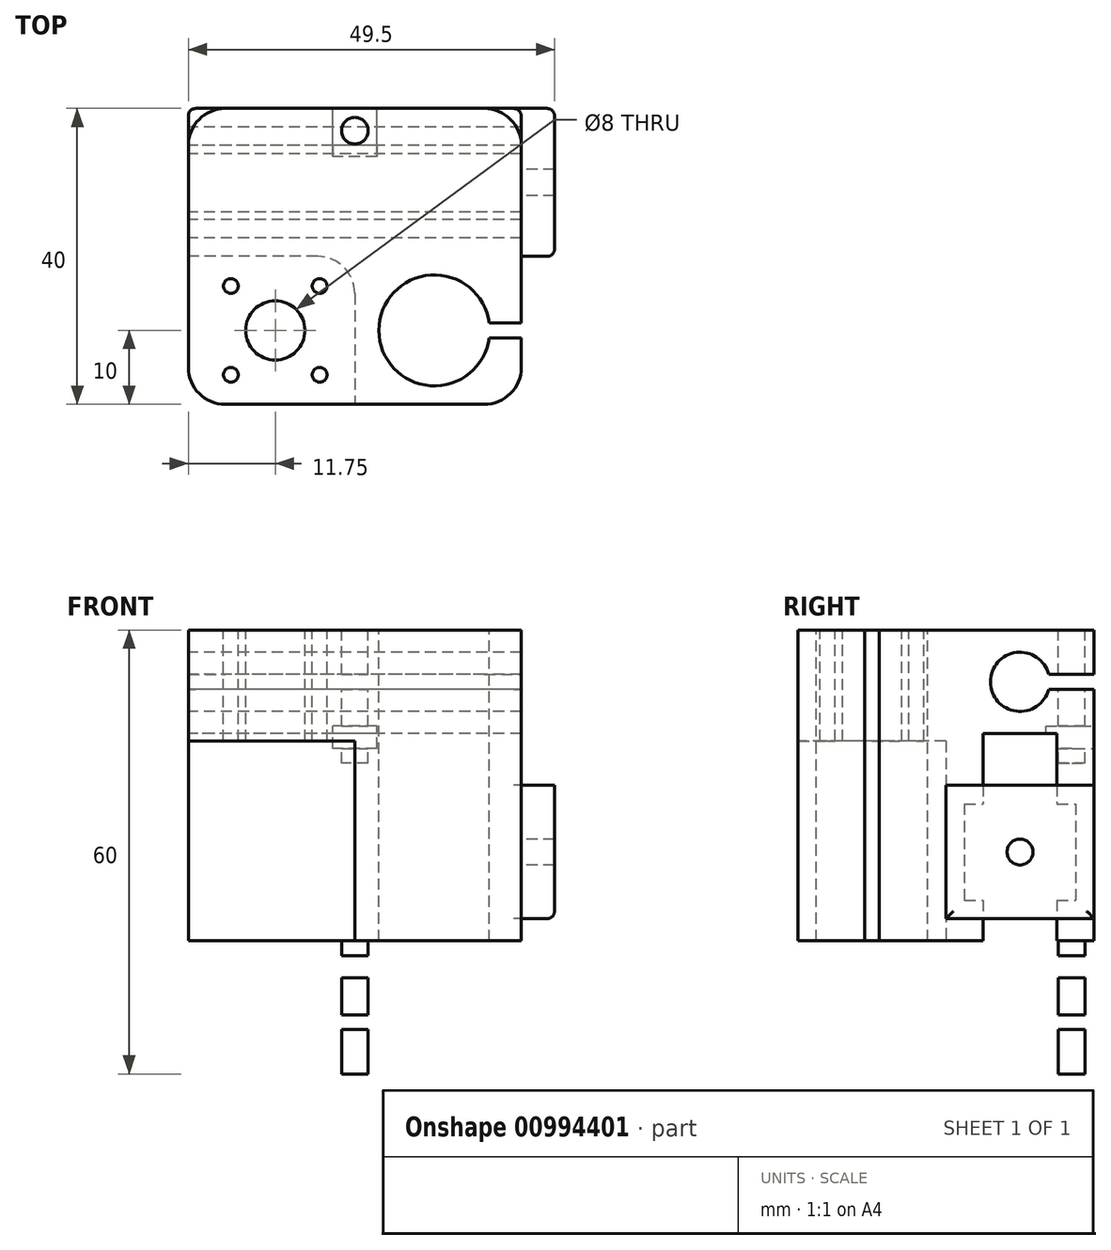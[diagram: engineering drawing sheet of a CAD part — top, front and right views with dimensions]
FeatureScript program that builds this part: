
annotation { "Feature Type Name" : "Feature", "Feature Type Description" : "" }
export const myFeature = defineFeature(function(context is Context, id is Id, definition is map)
    precondition{}
    {
        {
            var Q0;
            Q0=qCreatedBy(makeId("Top.planeOp"),FACE);
            var sketch = newSketch(context, id + "F0", { "sketchPlane" : qUnion([Q0])});
            skLineSegment(sketch, "E0.bottom", {"start": v(0, 0) * mm, "end": v(-45, 0) * mm});
            skLineSegment(sketch, "E0.top", {"start": v(0, 40) * mm, "end": v(-45, 40) * mm});
            skLineSegment(sketch, "E0.left", {"start": v(0, 0) * mm, "end": v(0, 40) * mm});
            skLineSegment(sketch, "E0.right", {"start": v(-45, 0) * mm, "end": v(-45, 40) * mm});
            skSolve(sketch);
        }
        {
            var Q0;
            Q0 = qSketchRegion(id + "F0", true);
            extrude(context, id + "F1", {"entities" : qUnion([Q0]), "depth" : 60 * mm, "offsetDistance" : 25 * mm});
        }
        {
            var Q0;
            Q0=makeQuery(id+"F1.opExtrude","CAP_FACE",FACE,{"disambiguationData":[OSD([sQuery(id+"F0.wireOp",EDGE,"E0.bottom"),sQuery(id+"F0.wireOp",EDGE,"E0.top"),sQuery(id+"F0.wireOp",EDGE,"E0.left"),sQuery(id+"F0.wireOp",EDGE,"E0.right")])],"isStart":false});
            var sketch = newSketch(context, id + "F2", { "sketchPlane" : qUnion([Q0])});
            skLineSegment(sketch, "E1", {"start": v(-45, 20) * mm, "end": v(0, 20) * mm});
            skLineSegment(sketch, "E2", {"start": v(0, 20) * mm, "end": v(-45, 0) * mm, "construction": true});
            skCircle(sketch, "E3", {"center": v(-33.25, 10) * mm, "radius": 4 * mm});
            skCircle(sketch, "E4", {"center": v(-11.75, 10) * mm, "radius": 4 * mm});
            skPoint(sketch, "E5", {"position": v(-22.5, 10) * mm});
            skPoint(sketch, "E6.0", {"position": v(-22.5, 0) * mm});
            skCircle(sketch, "E7", {"center": v(-11.75, 10) * mm, "radius": 7.5 * mm});
            skCircle(sketch, "E8", {"center": v(-39.25, 16) * mm, "radius": 1 * mm});
            skCircle(sketch, "E9", {"center": v(-27.25, 16) * mm, "radius": 1 * mm});
            skCircle(sketch, "E10", {"center": v(-27.25, 4) * mm, "radius": 1 * mm});
            skCircle(sketch, "E11", {"center": v(-39.25, 4) * mm, "radius": 1 * mm});
            skLineSegment(sketch, "E12", {"start": v(-39.25, 16) * mm, "end": v(-27.25, 4) * mm, "construction": true});
            skLineSegment(sketch, "E13", {"start": v(-4.25, 10) * mm, "end": v(0, 10) * mm});
            skLineSegment(sketch, "E14.0", {"start": v(-4.32, 9) * mm, "end": v(0, 9) * mm});
            skLineSegment(sketch, "E15.0", {"start": v(-4.32, 11) * mm, "end": v(0, 11) * mm});
            skCircle(sketch, "E16", {"center": v(-22.5, 37) * mm, "radius": 1.8 * mm});
            skPoint(sketch, "E16.centerSnap0", {"position": v(-22.5, 40) * mm});
            skSolve(sketch);
        }
        {
            var Q0;
            Q0=makeQuery(id+"F1.opExtrude","SWEPT_FACE",FACE,{"disambiguationData":[OSD([sQuery(id+"F0.wireOp",EDGE,"E0.right")])]});
            var sketch = newSketch(context, id + "F3", { "sketchPlane" : qUnion([Q0])});
            skLineSegment(sketch, "E17.0.0", {"start": v(-40, 0) * mm, "end": v(0, 0) * mm});
            skLineSegment(sketch, "E17.0.1", {"start": v(0, 0) * mm, "end": v(0, 60) * mm});
            skLineSegment(sketch, "E17.0.2", {"start": v(0, 60) * mm, "end": v(-40, 60) * mm});
            skLineSegment(sketch, "E17.0.3", {"start": v(-40, 60) * mm, "end": v(-40, 0) * mm});
            skLineSegment(sketch, "E18", {"start": v(-20, 60) * mm, "end": v(-20, 0) * mm});
            skLineSegment(sketch, "E19", {"start": v(-20, 60) * mm, "end": v(-40, 0) * mm, "construction": true});
            skArc(sketch, "E20", {"start": v(-33.87, 52) * mm, "mid": v(-26, 53) * mm, "end": v(-33.87, 54) * mm});
            skArc(sketch, "E21", {"start": v(-33.87, 6) * mm, "mid": v(-26, 7) * mm, "end": v(-33.87, 8) * mm});
            skPoint(sketch, "E22", {"position": v(-30, 30) * mm});
            skPoint(sketch, "E23", {"position": v(-40, 30) * mm});
            skLineSegment(sketch, "E24", {"start": v(-20, 45) * mm, "end": v(0, 45) * mm});
            skLineSegment(sketch, "E25.bottom", {"start": v(-25, 46) * mm, "end": v(-35, 46) * mm});
            skLineSegment(sketch, "E25.top", {"start": v(-25, 14) * mm, "end": v(-35, 14) * mm});
            skLineSegment(sketch, "E25.left", {"start": v(-25, 46) * mm, "end": v(-25, 14) * mm});
            skLineSegment(sketch, "E25.right", {"start": v(-35, 46) * mm, "end": v(-35, 14) * mm});
            skPoint(sketch, "E26", {"position": v(-30, 46) * mm});
            skLineSegment(sketch, "E27.bottom", {"start": v(-22.5, 36.5) * mm, "end": v(-37.5, 36.5) * mm});
            skLineSegment(sketch, "E27.top", {"start": v(-22.5, 23.5) * mm, "end": v(-37.5, 23.5) * mm});
            skLineSegment(sketch, "E27.left", {"start": v(-22.5, 36.5) * mm, "end": v(-22.5, 23.5) * mm});
            skLineSegment(sketch, "E27.right", {"start": v(-37.5, 36.5) * mm, "end": v(-37.5, 23.5) * mm});
            skPoint(sketch, "E28", {"position": v(-30, 36.5) * mm});
            skPoint(sketch, "E29", {"position": v(-37.5, 30) * mm});
            skLineSegment(sketch, "E30.bottom", {"start": v(-40, 52) * mm, "end": v(-33.87, 52) * mm});
            skLineSegment(sketch, "E30.top", {"start": v(-40, 54) * mm, "end": v(-33.87, 54) * mm});
            skLineSegment(sketch, "E30.left", {"start": v(-40, 52) * mm, "end": v(-40, 54) * mm});
            skLineSegment(sketch, "E30.right", {"start": v(-33.87, 52) * mm, "end": v(-33.87, 54) * mm});
            skLineSegment(sketch, "E31.bottom", {"start": v(-33.87, 6) * mm, "end": v(-40, 6) * mm});
            skLineSegment(sketch, "E31.top", {"start": v(-33.87, 8) * mm, "end": v(-40, 8) * mm});
            skLineSegment(sketch, "E31.left", {"start": v(-33.87, 6) * mm, "end": v(-33.87, 8) * mm});
            skLineSegment(sketch, "E31.right", {"start": v(-40, 6) * mm, "end": v(-40, 8) * mm});
            skSolve(sketch);
        }
        {
            var Q0;
            Q0=makeQuery(id+"F3.imprint","IMPRINT",FACE,{"disambiguationData":[TD([[makeQuery(id+"F3.imprint","IMPRINT",EDGE,{"derivedFrom":sQuery(id+"F3.wireOp",EDGE,"E20")}),1.0]])]});
            var Q1;
            Q1=makeQuery(id+"F3.imprint","IMPRINT",FACE,{"disambiguationData":[TD([[makeQuery(id+"F3.imprint","IMPRINT",EDGE,{"derivedFrom":sQuery(id+"F3.wireOp",EDGE,"E21")}),1.0]])]});
            var Q2;
            Q2=makeQuery(id+"F3.imprint","IMPRINT",FACE,{"disambiguationData":[TD([[makeQuery(id+"F3.imprint","IMPRINT",EDGE,{"derivedFrom":sQuery(id+"F3.wireOp",EDGE,"E25.bottom")}),1.0]])]});
            var Q3;
            {var subQ0=sQuery(id+"F3.wireOp",EDGE,"E27.bottom");var subQ1=sQuery(id+"F3.wireOp",EDGE,"E25.left");var subQ2=makeQuery(id+"F3.imprint","INTERSECT",VERTEX,{"derivedFrom":[subQ1,subQ0]});Q3=makeQuery(id+"F3.imprint","IMPRINT",FACE,{"disambiguationData":[TD([[makeQuery(id+"F3.imprint","IMPRINT",EDGE,{"disambiguationData":[TD([[subQ2,-1.0]])],"derivedFrom":subQ1}),-1.0]])]});}
            var Q4;
            {var subQ5=sQuery(id+"F3.wireOp",EDGE,"E27.left");Q4=makeQuery(id+"F3.imprint","IMPRINT",FACE,{"disambiguationData":[TD([[makeQuery(id+"F3.imprint","IMPRINT",EDGE,{"derivedFrom":subQ5}),-1.0]])]});}
            var Q5;
            {var subQ5=sQuery(id+"F3.wireOp",EDGE,"E27.right");Q5=makeQuery(id+"F3.imprint","IMPRINT",FACE,{"disambiguationData":[TD([[makeQuery(id+"F3.imprint","IMPRINT",EDGE,{"derivedFrom":subQ5}),1.0]])]});}
            var Q6;
            {var subQ0=sQuery(id+"F3.wireOp",EDGE,"E25.top");Q6=makeQuery(id+"F3.imprint","IMPRINT",FACE,{"disambiguationData":[TD([[makeQuery(id+"F3.imprint","IMPRINT",EDGE,{"derivedFrom":subQ0}),-1.0]])]});}
            var Q7;
            {var subQ0=sQuery(id+"F3.wireOp",EDGE,"E30.bottom");Q7=makeQuery(id+"F3.imprint","IMPRINT",FACE,{"disambiguationData":[TD([[makeQuery(id+"F3.imprint","IMPRINT",EDGE,{"derivedFrom":subQ0}),1.0]])]});}
            var Q8;
            {var subQ0=sQuery(id+"F3.wireOp",EDGE,"E31.bottom");Q8=makeQuery(id+"F3.imprint","IMPRINT",FACE,{"disambiguationData":[TD([[makeQuery(id+"F3.imprint","IMPRINT",EDGE,{"derivedFrom":subQ0}),-1.0]])]});}
            extrude(context, id + "F4", {"entities" : qUnion([Q0, Q1, Q2, Q3, Q4, Q5, Q6, Q7, Q8]), "operationType" : NewBodyOperationType.REMOVE, "oppositeDirection" : true, "depth" : 45 * mm, "offsetDistance" : 25 * mm});
        }
        {
            var Q0;
            {var subQ5=sQuery(id+"F3.wireOp",EDGE,"E24");Q0=makeQuery(id+"F3.imprint","IMPRINT",FACE,{"disambiguationData":[TD([[makeQuery(id+"F3.imprint","IMPRINT",EDGE,{"derivedFrom":subQ5}),-1.0]])]});}
            extrude(context, id + "F5", {"entities" : qUnion([Q0]), "operationType" : NewBodyOperationType.REMOVE, "oppositeDirection" : true, "depth" : 22.5 * mm, "offsetDistance" : 25 * mm});
        }
        {
            var Q0;
            Q0=makeQuery(id+"F2.imprint","IMPRINT",FACE,{"disambiguationData":[TD([[makeQuery(id+"F2.imprint","IMPRINT",EDGE,{"derivedFrom":sQuery(id+"F2.wireOp",EDGE,"E3")}),1.0]])]});
            var Q1;
            Q1=makeQuery(id+"F2.imprint","IMPRINT",FACE,{"disambiguationData":[TD([[makeQuery(id+"F2.imprint","IMPRINT",EDGE,{"derivedFrom":sQuery(id+"F2.wireOp",EDGE,"E9")}),1.0]])]});
            var Q2;
            Q2=makeQuery(id+"F2.imprint","IMPRINT",FACE,{"disambiguationData":[TD([[makeQuery(id+"F2.imprint","IMPRINT",EDGE,{"derivedFrom":sQuery(id+"F2.wireOp",EDGE,"E8")}),1.0]])]});
            var Q3;
            Q3=makeQuery(id+"F2.imprint","IMPRINT",FACE,{"disambiguationData":[TD([[makeQuery(id+"F2.imprint","IMPRINT",EDGE,{"derivedFrom":sQuery(id+"F2.wireOp",EDGE,"E10")}),1.0]])]});
            var Q4;
            Q4=makeQuery(id+"F2.imprint","IMPRINT",FACE,{"disambiguationData":[TD([[makeQuery(id+"F2.imprint","IMPRINT",EDGE,{"derivedFrom":sQuery(id+"F2.wireOp",EDGE,"E11")}),1.0]])]});
            var Q5;
            Q5=makeQuery(id+"F2.imprint","IMPRINT",FACE,{"disambiguationData":[TD([[makeQuery(id+"F2.imprint","IMPRINT",EDGE,{"derivedFrom":sQuery(id+"F2.wireOp",EDGE,"E4")}),-1.0]])]});
            var Q6;
            Q6=makeQuery(id+"F2.imprint","IMPRINT",FACE,{"disambiguationData":[TD([[makeQuery(id+"F2.imprint","IMPRINT",EDGE,{"derivedFrom":sQuery(id+"F2.wireOp",EDGE,"E4")}),1.0]])]});
            var Q7;
            {var subQ0=sQuery(id+"F2.wireOp",EDGE,"E13");Q7=makeQuery(id+"F2.imprint","IMPRINT",FACE,{"disambiguationData":[TD([[makeQuery(id+"F2.imprint","IMPRINT",EDGE,{"derivedFrom":subQ0}),-1.0]])]});}
            var Q8;
            {var subQ0=sQuery(id+"F2.wireOp",EDGE,"E13");Q8=makeQuery(id+"F2.imprint","IMPRINT",FACE,{"disambiguationData":[TD([[makeQuery(id+"F2.imprint","IMPRINT",EDGE,{"derivedFrom":subQ0}),1.0]])]});}
            extrude(context, id + "F6", {"entities" : qUnion([Q0, Q1, Q2, Q3, Q4, Q5, Q6, Q7, Q8]), "operationType" : NewBodyOperationType.REMOVE, "oppositeDirection" : true, "depth" : 60 * mm, "offsetDistance" : 25 * mm});
        }
        {
            var Q0;
            {var subQ10=sQuery(id+"F0.wireOp",EDGE,"E0.left");var subQ11=sQuery(id+"F0.wireOp",EDGE,"E0.top");Q0=makeQuery(id+"F6.boolean.opBoolean","SPLIT",FACE,{"disambiguationData":[TD([makeQuery(id+"F1.opExtrude","SWEPT_FACE",FACE,{"disambiguationData":[OSD([subQ11])]})])],"derivedFrom":makeQuery(id+"F1.opExtrude","SWEPT_FACE",FACE,{"disambiguationData":[OSD([subQ10])]})});}
            var sketch = newSketch(context, id + "F7", { "sketchPlane" : qUnion([Q0])});
            skLineSegment(sketch, "E32.0", {"start": v(37.5, 36.5) * mm, "end": v(37.5, 23.5) * mm});
            skLineSegment(sketch, "E33.0", {"start": v(22.5, 36.5) * mm, "end": v(37.5, 36.5) * mm});
            skLineSegment(sketch, "E34.0", {"start": v(22.5, 23.5) * mm, "end": v(37.5, 23.5) * mm});
            skLineSegment(sketch, "E35.0", {"start": v(22.5, 36.5) * mm, "end": v(22.5, 23.5) * mm});
            skLineSegment(sketch, "E36.0", {"start": v(20, 39) * mm, "end": v(40, 39) * mm});
            skLineSegment(sketch, "E36.1", {"start": v(20, 39) * mm, "end": v(20, 21) * mm});
            skLineSegment(sketch, "E36.2", {"start": v(20, 21) * mm, "end": v(40, 21) * mm});
            skLineSegment(sketch, "E36.3", {"start": v(40, 39) * mm, "end": v(40, 21) * mm});
            skLineSegment(sketch, "E37", {"start": v(22.5, 36.5) * mm, "end": v(37.5, 23.5) * mm, "construction": true});
            skCircle(sketch, "E38", {"center": v(30, 30) * mm, "radius": 1.75 * mm});
            skSolve(sketch);
        }
        {
            var Q0;
            {var subQ5=sQuery(id+"F7.wireOp",EDGE,"E32.0");Q0=makeQuery(id+"F7.imprint","IMPRINT",FACE,{"disambiguationData":[TD([[makeQuery(id+"F7.imprint","IMPRINT",EDGE,{"derivedFrom":subQ5}),-1.0]])]});}
            var Q1;
            {var subQ8=sQuery(id+"F7.wireOp",EDGE,"E35.0");Q1=makeQuery(id+"F7.imprint","IMPRINT",FACE,{"disambiguationData":[TD([[makeQuery(id+"F7.imprint","IMPRINT",EDGE,{"derivedFrom":subQ8}),-1.0]])]});}
            var Q2;
            {var subQ0=sQuery(id+"F7.wireOp",EDGE,"E33.0");var subQ1=sQuery(id+"F3.wireOp",EDGE,"E25.left");var subQ2=sQuery(id+"F3.wireOp",EDGE,"E25.bottom");var subQ4=makeQuery(id+"F4.boolean.opBoolean","COPY",EDGE,{"derivedFrom":makeQuery(id+"F4.opExtrude","CAP_EDGE",EDGE,{"disambiguationData":[OSD([subQ1]),TDD([makeQuery(id+"F3.imprint","IMPRINT",EDGE,{"disambiguationData":[TD([[makeQuery(id+"F3.imprint","INTERSECT",VERTEX,{"derivedFrom":[subQ2,subQ1]}),-1.0]])],"derivedFrom":subQ1})])],"isStart":false})});var subQ5=makeQuery(id+"F7.imprint","INTERSECT",VERTEX,{"derivedFrom":[subQ4,subQ0]});Q2=makeQuery(id+"F7.imprint","IMPRINT",FACE,{"disambiguationData":[TD([[makeQuery(id+"F7.imprint","IMPRINT",EDGE,{"disambiguationData":[TD([[subQ5,-1.0]])],"derivedFrom":subQ0}),1.0]])]});}
            var Q3;
            {var subQ1=sQuery(id+"F7.wireOp",EDGE,"E32.0");Q3=makeQuery(id+"F7.imprint","IMPRINT",FACE,{"disambiguationData":[TD([[makeQuery(id+"F7.imprint","IMPRINT",EDGE,{"derivedFrom":subQ1}),1.0]])]});}
            var Q4;
            {var subQ0=sQuery(id+"F7.wireOp",EDGE,"E34.0");var subQ1=sQuery(id+"F3.wireOp",EDGE,"E25.left");var subQ2=sQuery(id+"F3.wireOp",EDGE,"E25.top");var subQ4=makeQuery(id+"F4.boolean.opBoolean","COPY",EDGE,{"derivedFrom":makeQuery(id+"F4.opExtrude","CAP_EDGE",EDGE,{"disambiguationData":[OSD([subQ1]),TDD([makeQuery(id+"F3.imprint","IMPRINT",EDGE,{"disambiguationData":[TD([[makeQuery(id+"F3.imprint","INTERSECT",VERTEX,{"derivedFrom":[subQ2,subQ1]}),1.0]])],"derivedFrom":subQ1})])],"isStart":false})});var subQ5=makeQuery(id+"F7.imprint","INTERSECT",VERTEX,{"derivedFrom":[subQ4,subQ0]});Q4=makeQuery(id+"F7.imprint","IMPRINT",FACE,{"disambiguationData":[TD([[makeQuery(id+"F7.imprint","IMPRINT",EDGE,{"disambiguationData":[TD([[subQ5,-1.0]])],"derivedFrom":subQ0}),-1.0]])]});}
            extrude(context, id + "F8", {"entities" : qUnion([Q0, Q1, Q2, Q3, Q4]), "operationType" : NewBodyOperationType.ADD, "depth" : 4.5 * mm, "offsetDistance" : 25 * mm});
        }
        {
            var Q0;
            Q0=makeQuery(id+"F2.imprint","IMPRINT",FACE,{"disambiguationData":[TD([[makeQuery(id+"F2.imprint","IMPRINT",EDGE,{"derivedFrom":sQuery(id+"F2.wireOp",EDGE,"E16")}),1.0]])]});
            extrude(context, id + "F9", {"entities" : qUnion([Q0]), "operationType" : NewBodyOperationType.REMOVE, "oppositeDirection" : true, "depth" : 18 * mm, "offsetDistance" : 25 * mm});
        }
        {
            var Q0;
            Q0=makeQuery(id+"F1.opExtrude","CAP_FACE",FACE,{"disambiguationData":[OSD([sQuery(id+"F0.wireOp",EDGE,"E0.bottom"),sQuery(id+"F0.wireOp",EDGE,"E0.top"),sQuery(id+"F0.wireOp",EDGE,"E0.left"),sQuery(id+"F0.wireOp",EDGE,"E0.right")])],"isStart":true});
            var sketch = newSketch(context, id + "F10", { "sketchPlane" : qUnion([Q0])});
            skCircle(sketch, "E39.0.0", {"center": v(-22.5, -37) * mm, "radius": 1.8 * mm});
            skSolve(sketch);
        }
        {
            var Q0;
            Q0=makeQuery(id+"F10.imprint","IMPRINT",FACE,{"disambiguationData":[TD([[makeQuery(id+"F10.imprint","IMPRINT",EDGE,{"derivedFrom":sQuery(id+"F10.wireOp",EDGE,"E39.0.0")}),-1.0]])]});
            extrude(context, id + "F11", {"entities" : qUnion([Q0]), "operationType" : NewBodyOperationType.REMOVE, "oppositeDirection" : true, "depth" : 18 * mm, "offsetDistance" : 25 * mm});
        }
        {
            var Q0;
            Q0=makeQuery(id+"F8.boolean.opBoolean","MERGE",FACE,{"derivedFrom":[makeQuery(id+"F4.boolean.opBoolean","SPLIT",FACE,{"disambiguationData":[TD([makeQuery(id+"F4.opExtrude","SWEPT_FACE",FACE,{"disambiguationData":[OSD([sQuery(id+"F3.wireOp",EDGE,"E30.bottom")])]})])],"derivedFrom":makeQuery(id+"F1.opExtrude","SWEPT_FACE",FACE,{"disambiguationData":[OSD([sQuery(id+"F0.wireOp",EDGE,"E0.top")])]})}),makeQuery(id+"F8.opExtrude","SWEPT_FACE",FACE,{"disambiguationData":[OSD([sQuery(id+"F7.wireOp",EDGE,"E36.3")])]})]});
            var sketch = newSketch(context, id + "F12", { "sketchPlane" : qUnion([Q0])});
            skPoint(sketch, "E40.0", {"position": v(22.5, 60) * mm});
            skPoint(sketch, "E41.0", {"position": v(22.5, 0) * mm});
            skLineSegment(sketch, "E42.bottom", {"start": v(19.5, 16) * mm, "end": v(25.5, 16) * mm});
            skLineSegment(sketch, "E42.top", {"start": v(19.5, 13) * mm, "end": v(25.5, 13) * mm});
            skLineSegment(sketch, "E42.left", {"start": v(19.5, 16) * mm, "end": v(19.5, 13) * mm});
            skLineSegment(sketch, "E42.right", {"start": v(25.5, 16) * mm, "end": v(25.5, 13) * mm});
            skLineSegment(sketch, "E43.bottom", {"start": v(19.5, 44) * mm, "end": v(25.5, 44) * mm});
            skLineSegment(sketch, "E43.top", {"start": v(19.5, 47) * mm, "end": v(25.5, 47) * mm});
            skLineSegment(sketch, "E43.left", {"start": v(19.5, 44) * mm, "end": v(19.5, 47) * mm});
            skLineSegment(sketch, "E43.right", {"start": v(25.5, 44) * mm, "end": v(25.5, 47) * mm});
            skPoint(sketch, "E44", {"position": v(22.5, 13) * mm});
            skSolve(sketch);
        }
        {
            var Q0;
            {var subQ0=sQuery(id+"F12.wireOp",EDGE,"E43.bottom");var subQ1=sQuery(id+"F12.wireOp",EDGE,"b4135b6c-352a-4d6d-b6e8-f4d1ccfc09f6");var subQ2=makeQuery(id+"F12.imprint","INTERSECT",VERTEX,{"derivedFrom":[subQ1,subQ0]});Q0=makeQuery(id+"F12.imprint","IMPRINT",FACE,{"disambiguationData":[TD([[makeQuery(id+"F12.imprint","IMPRINT",EDGE,{"disambiguationData":[TD([[subQ2,1.0]])],"derivedFrom":subQ1}),-1.0]])]});}
            var Q1;
            {var subQ5=sQuery(id+"F12.wireOp",EDGE,"E43.right");Q1=makeQuery(id+"F12.imprint","IMPRINT",FACE,{"disambiguationData":[TD([[makeQuery(id+"F12.imprint","IMPRINT",EDGE,{"derivedFrom":subQ5}),1.0]])]});}
            var Q2;
            {var subQ5=sQuery(id+"F12.wireOp",EDGE,"E43.left");Q2=makeQuery(id+"F12.imprint","IMPRINT",FACE,{"disambiguationData":[TD([[makeQuery(id+"F12.imprint","IMPRINT",EDGE,{"derivedFrom":subQ5}),-1.0]])]});}
            var Q3;
            {var subQ5=sQuery(id+"F12.wireOp",EDGE,"E42.right");Q3=makeQuery(id+"F12.imprint","IMPRINT",FACE,{"disambiguationData":[TD([[makeQuery(id+"F12.imprint","IMPRINT",EDGE,{"derivedFrom":subQ5}),-1.0]])]});}
            var Q4;
            {var subQ0=sQuery(id+"F12.wireOp",EDGE,"E42.top");var subQ1=sQuery(id+"F12.wireOp",EDGE,"b4135b6c-352a-4d6d-b6e8-f4d1ccfc09f6");var subQ2=makeQuery(id+"F12.imprint","INTERSECT",VERTEX,{"derivedFrom":[subQ1,subQ0]});Q4=makeQuery(id+"F12.imprint","IMPRINT",FACE,{"disambiguationData":[TD([[makeQuery(id+"F12.imprint","IMPRINT",EDGE,{"disambiguationData":[TD([[subQ2,1.0]])],"derivedFrom":subQ1}),-1.0]])]});}
            var Q5;
            {var subQ5=sQuery(id+"F12.wireOp",EDGE,"E42.left");Q5=makeQuery(id+"F12.imprint","IMPRINT",FACE,{"disambiguationData":[TD([[makeQuery(id+"F12.imprint","IMPRINT",EDGE,{"derivedFrom":subQ5}),1.0]])]});}
            extrude(context, id + "F13", {"entities" : qUnion([Q0, Q1, Q2, Q3, Q4, Q5]), "operationType" : NewBodyOperationType.REMOVE, "oppositeDirection" : true, "depth" : 6.5 * mm, "offsetDistance" : 25 * mm});
        }
        {
            var Q0;
            Q0=makeQuery(id+"F1.opExtrude","SWEPT_EDGE",EDGE,{"disambiguationData":[OSD([sQuery(id+"F0.wireOp",EDGE,"E0.bottom"),sQuery(id+"F0.wireOp",EDGE,"E0.right")])]});
            var Q1;
            Q1=makeQuery(id+"F5.boolean.opBoolean","COPY",EDGE,{"derivedFrom":makeQuery(id+"F5.opExtrude","CAP_EDGE",EDGE,{"disambiguationData":[OSD([sQuery(id+"F3.wireOp",EDGE,"E17.0.1")])],"isStart":false})});
            var Q2;
            Q2=makeQuery(id+"F5.boolean.opBoolean","COPY",EDGE,{"derivedFrom":makeQuery(id+"F5.opExtrude","CAP_EDGE",EDGE,{"disambiguationData":[OSD([sQuery(id+"F3.wireOp",EDGE,"E18")])],"isStart":false})});
            var Q3;
            Q3=makeQuery(id+"F1.opExtrude","SWEPT_EDGE",EDGE,{"disambiguationData":[OSD([sQuery(id+"F0.wireOp",EDGE,"E0.bottom"),sQuery(id+"F0.wireOp",EDGE,"E0.left")])]});
            var Q4;
            {var subQ0=sQuery(id+"F0.wireOp",EDGE,"E0.left");var subQ1=sQuery(id+"F0.wireOp",EDGE,"E0.top");Q4=makeQuery(id+"F4.boolean.opBoolean","SPLIT",EDGE,{"disambiguationData":[TD([makeQuery(id+"F4.opExtrude","SWEPT_FACE",FACE,{"disambiguationData":[OSD([sQuery(id+"F3.wireOp",EDGE,"E30.top")])]})])],"derivedFrom":makeQuery(id+"F1.opExtrude","SWEPT_EDGE",EDGE,{"disambiguationData":[OSD([subQ1,subQ0])]})});}
            var Q5;
            {var subQ0=sQuery(id+"F0.wireOp",EDGE,"E0.left");var subQ1=sQuery(id+"F0.wireOp",EDGE,"E0.top");Q5=makeQuery(id+"F4.boolean.opBoolean","SPLIT",EDGE,{"disambiguationData":[TD([makeQuery(id+"F4.opExtrude","SWEPT_FACE",FACE,{"disambiguationData":[OSD([sQuery(id+"F3.wireOp",EDGE,"E31.bottom")])]})])],"derivedFrom":makeQuery(id+"F1.opExtrude","SWEPT_EDGE",EDGE,{"disambiguationData":[OSD([subQ1,subQ0])]})});}
            var Q6;
            {var subQ0=sQuery(id+"F0.wireOp",EDGE,"E0.right");var subQ1=sQuery(id+"F0.wireOp",EDGE,"E0.top");Q6=makeQuery(id+"F4.boolean.opBoolean","SPLIT",EDGE,{"disambiguationData":[TD([makeQuery(id+"F4.opExtrude","SWEPT_FACE",FACE,{"disambiguationData":[OSD([sQuery(id+"F3.wireOp",EDGE,"E31.bottom")])]})])],"derivedFrom":makeQuery(id+"F1.opExtrude","SWEPT_EDGE",EDGE,{"disambiguationData":[OSD([subQ1,subQ0])]})});}
            var Q7;
            {var subQ0=sQuery(id+"F0.wireOp",EDGE,"E0.right");var subQ1=sQuery(id+"F0.wireOp",EDGE,"E0.top");Q7=makeQuery(id+"F4.boolean.opBoolean","SPLIT",EDGE,{"disambiguationData":[TD([makeQuery(id+"F4.opExtrude","SWEPT_FACE",FACE,{"disambiguationData":[OSD([sQuery(id+"F3.wireOp",EDGE,"E30.top")])]})])],"derivedFrom":makeQuery(id+"F1.opExtrude","SWEPT_EDGE",EDGE,{"disambiguationData":[OSD([subQ1,subQ0])]})});}
            fillet(context, id + "F14", {"entities" : qUnion([Q0, Q1, Q2, Q3, Q4, Q5, Q6, Q7]), "tangentPropagation" : true, "radius" : 5 * mm, "defaultsChanged" : false, "vertexSettings" : [], "allowEdgeOverflow" : false});
        }
        {
            var Q0;
            Q0=makeQuery(id+"F5.boolean.opBoolean","COPY",EDGE,{"derivedFrom":makeQuery(id+"F5.opExtrude","SWEPT_EDGE",EDGE,{"disambiguationData":[OSD([sQuery(id+"F3.wireOp",EDGE,"E17.0.0"),sQuery(id+"F3.wireOp",EDGE,"E18")])]})});
            var Q1;
            Q1=makeQuery(id+"F1.opExtrude","CAP_EDGE",EDGE,{"disambiguationData":[OSD([sQuery(id+"F0.wireOp",EDGE,"E0.top")])],"isStart":true});
            var Q2;
            Q2=makeQuery(id+"F6.boolean.opBoolean","COPY",EDGE,{"derivedFrom":makeQuery(id+"F6.opExtrude","CAP_EDGE",EDGE,{"disambiguationData":[OSD([sQuery(id+"F2.wireOp",EDGE,"E7")])],"isStart":false})});
            var Q3;
            Q3=makeQuery(id+"F5.boolean.opBoolean","COPY",EDGE,{"derivedFrom":makeQuery(id+"F5.opExtrude","CAP_EDGE",EDGE,{"disambiguationData":[OSD([sQuery(id+"F3.wireOp",EDGE,"E18")])],"isStart":true})});
            var Q4;
            {var subQ0=makeQuery(id+"F4.opExtrude","SWEPT_FACE",FACE,{"disambiguationData":[OSD([sQuery(id+"F3.wireOp",EDGE,"E31.top")])]});var subQ1=sQuery(id+"F0.wireOp",EDGE,"E0.left");var subQ3=sQuery(id+"F0.wireOp",EDGE,"E0.top");Q4=makeQuery(id+"F8.boolean.opBoolean","SPLIT",EDGE,{"disambiguationData":[TD([makeQuery(id+"F4.boolean.opBoolean","COPY",FACE,{"derivedFrom":subQ0})])],"derivedFrom":makeQuery(id+"F4.boolean.opBoolean","SPLIT",EDGE,{"disambiguationData":[TD([makeQuery(id+"F4.opExtrude","SWEPT_FACE",FACE,{"disambiguationData":[OSD([sQuery(id+"F3.wireOp",EDGE,"E30.bottom")])]})])],"derivedFrom":makeQuery(id+"F1.opExtrude","SWEPT_EDGE",EDGE,{"disambiguationData":[OSD([subQ3,subQ1])]})})});}
            var Q5;
            {var subQ0=makeQuery(id+"F4.opExtrude","SWEPT_FACE",FACE,{"disambiguationData":[OSD([sQuery(id+"F3.wireOp",EDGE,"E30.bottom")])]});var subQ1=sQuery(id+"F0.wireOp",EDGE,"E0.left");var subQ3=sQuery(id+"F0.wireOp",EDGE,"E0.top");Q5=makeQuery(id+"F8.boolean.opBoolean","SPLIT",EDGE,{"disambiguationData":[TD([makeQuery(id+"F4.boolean.opBoolean","COPY",FACE,{"derivedFrom":subQ0})])],"derivedFrom":makeQuery(id+"F4.boolean.opBoolean","SPLIT",EDGE,{"disambiguationData":[TD([subQ0])],"derivedFrom":makeQuery(id+"F1.opExtrude","SWEPT_EDGE",EDGE,{"disambiguationData":[OSD([subQ3,subQ1])]})})});}
            var Q6;
            Q6=makeQuery(id+"F8.opExtrude","CAP_EDGE",EDGE,{"disambiguationData":[OSD([sQuery(id+"F7.wireOp",EDGE,"E36.3")])],"isStart":false});
            var Q7;
            Q7=makeQuery(id+"F8.opExtrude","CAP_EDGE",EDGE,{"disambiguationData":[OSD([sQuery(id+"F7.wireOp",EDGE,"E36.1")])],"isStart":false});
            var Q8;
            Q8=makeQuery(id+"F8.opExtrude","CAP_EDGE",EDGE,{"disambiguationData":[OSD([sQuery(id+"F7.wireOp",EDGE,"E36.2")])],"isStart":false});
            var Q9;
            Q9=makeQuery(id+"F4.boolean.opBoolean","COPY",EDGE,{"derivedFrom":makeQuery(id+"F4.opExtrude","CAP_EDGE",EDGE,{"disambiguationData":[OSD([sQuery(id+"F3.wireOp",EDGE,"E20")])],"isStart":true})});
            var Q10;
            Q10=makeQuery(id+"F4.boolean.opBoolean","COPY",EDGE,{"derivedFrom":makeQuery(id+"F4.opExtrude","CAP_EDGE",EDGE,{"disambiguationData":[OSD([sQuery(id+"F3.wireOp",EDGE,"E21")])],"isStart":true})});
            var Q11;
            {var subQ0=sQuery(id+"F0.wireOp",EDGE,"E0.top");var subQ1=sQuery(id+"F0.wireOp",EDGE,"E0.right");Q11=makeQuery(id+"F4.boolean.opBoolean","SPLIT",EDGE,{"disambiguationData":[TD([makeQuery(id+"F4.opExtrude","SWEPT_FACE",FACE,{"disambiguationData":[OSD([sQuery(id+"F3.wireOp",EDGE,"E30.bottom")])]})])],"derivedFrom":makeQuery(id+"F1.opExtrude","SWEPT_EDGE",EDGE,{"disambiguationData":[OSD([subQ0,subQ1])]})});}
            fillet(context, id + "F15", {"entities" : qUnion([Q0, Q1, Q2, Q3, Q4, Q5, Q6, Q7, Q8, Q9, Q10, Q11]), "tangentPropagation" : true, "radius" : 1 * mm, "defaultsChanged" : false, "vertexSettings" : [], "allowEdgeOverflow" : false});
        }
    });
